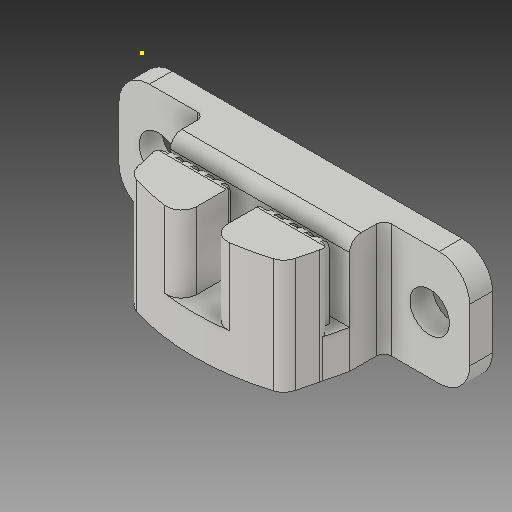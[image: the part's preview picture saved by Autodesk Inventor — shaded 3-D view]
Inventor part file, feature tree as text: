
AUTODESK INVENTOR PART (.ipt)
format: ipt  version: 2018 (Build 220112000, 112)  size: 308,224 bytes
history: native  units: mm
features: sketch x12, other x3
ambient origin geometry x8: Origin, YZ Plane, XZ Plane, XY Plane, X Axis, Y Axis, Z Axis, Center Point
bodies: Solid1 (feature_tree)
feature tree (15):
  other  "X Belt Clamp_MIR.ipt"
  other  "Solid1::X Belt Clamp_MIR.ipt"
  other  "TaggingFeature1"
  sketch  "Sketch1"  dims[d0=10.0mm]
  sketch  "Sketch2"
  sketch  "Sketch3"
  sketch  "Sketch4"
  sketch  "Sketch5"
  sketch  "Sketch6"
  sketch  "Sketch7"
  sketch  "Sketch8"
  sketch  "Sketch9"
  sketch  "Sketch10"
  sketch  "Sketch11"
  sketch  "Sketch12"
